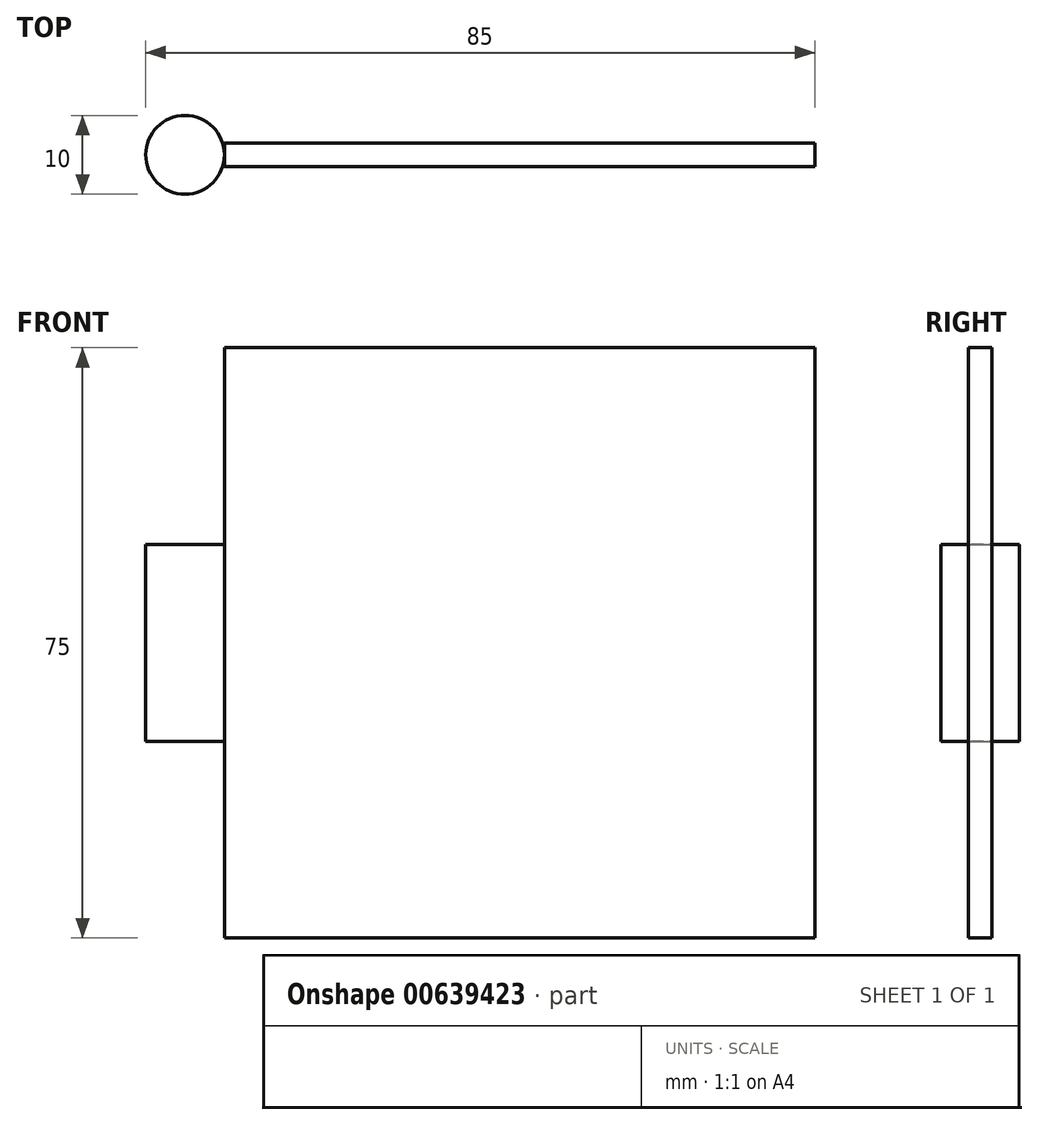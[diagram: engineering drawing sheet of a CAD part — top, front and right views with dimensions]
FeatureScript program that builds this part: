
annotation { "Feature Type Name" : "Feature", "Feature Type Description" : "" }
export const myFeature = defineFeature(function(context is Context, id is Id, definition is map)
    precondition{}
    {
        {
            var Q0;
            Q0=qCreatedBy(makeId("Front.planeOp"),FACE);
            var sketch = newSketch(context, id + "F0", { "sketchPlane" : qUnion([Q0])});
            skLineSegment(sketch, "E0.bottom", {"start": v(0, 0) * mm, "end": v(75, 0) * mm});
            skLineSegment(sketch, "E0.top", {"start": v(0, 75) * mm, "end": v(75, 75) * mm});
            skLineSegment(sketch, "E0.left", {"start": v(0, 0) * mm, "end": v(0, 75) * mm});
            skLineSegment(sketch, "E0.right", {"start": v(75, 0) * mm, "end": v(75, 75) * mm});
            skSolve(sketch);
        }
        {
            var Q0;
            Q0=makeQuery(id+"F0.imprint","IMPRINT",FACE,{"disambiguationData":[TD([[makeQuery(id+"F0.imprint","IMPRINT",EDGE,{"derivedFrom":sQuery(id+"F0.wireOp",EDGE,"E0.bottom")}),1.0]])]});
            extrude(context, id + "F1", {"entities" : qUnion([Q0]), "depth" : 3 * mm, "offsetDistance" : 25 * mm});
        }
        {
            var Q0;
            Q0=qCreatedBy(makeId("Top.planeOp"),FACE);
            cPlane(context, id + "F2", {"entities" : qUnion([Q0]), "cplaneType" : CPlaneType.OFFSET, "offset" : 37.5 * mm, "width" : 150 * mm, "height" : 150 * mm});
        }
        {
            var Q0;
            Q0=qCreatedBy(id+"F2.planeOp",FACE);
            var sketch = newSketch(context, id + "F3", { "sketchPlane" : qUnion([Q0])});
            skPoint(sketch, "E1.0", {"position": v(0, -1.5) * mm});
            skLineSegment(sketch, "E2", {"start": v(0, -1.5) * mm, "end": v(-5, -1.5) * mm});
            skCircle(sketch, "E3", {"center": v(-5, -1.5) * mm, "radius": 5 * mm});
            skSolve(sketch);
        }
        {
            var Q0;
            Q0=makeQuery(id+"F3.imprint","IMPRINT",FACE,{"disambiguationData":[TD([[makeQuery(id+"F3.imprint","IMPRINT",EDGE,{"derivedFrom":sQuery(id+"F3.wireOp",EDGE,"E3")}),1.0]])]});
            extrude(context, id + "F4", {"entities" : qUnion([Q0]), "operationType" : NewBodyOperationType.ADD, "depth" : 25 * mm, "offsetDistance" : 25 * mm, "symmetric" : true});
        }
    });
